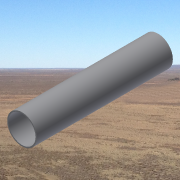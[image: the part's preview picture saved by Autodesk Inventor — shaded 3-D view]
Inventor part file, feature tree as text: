
AUTODESK INVENTOR PART (.ipt)
format: ipt  version: 2014 SP1 (Build 180222100, 222)  size: 126,976 bytes
history: native  units: in
note: dims shown in document units (in); Inventor stores cm internally (conversion verified against a paired STEP export)
features: extrude x1, sketch x1
ambient origin geometry x8: Origin, YZ Plane, XZ Plane, XY Plane, X Axis, Y Axis, Z Axis, Center Point
bodies: Solid1 (feature_tree)
feature tree (2):
  extrude  "Extrusion1"  Depth=19.685in
  sketch  "Sketch1"  dims[d0=3.937in d1=0.175in d2=19.685in d3=0.0in]
